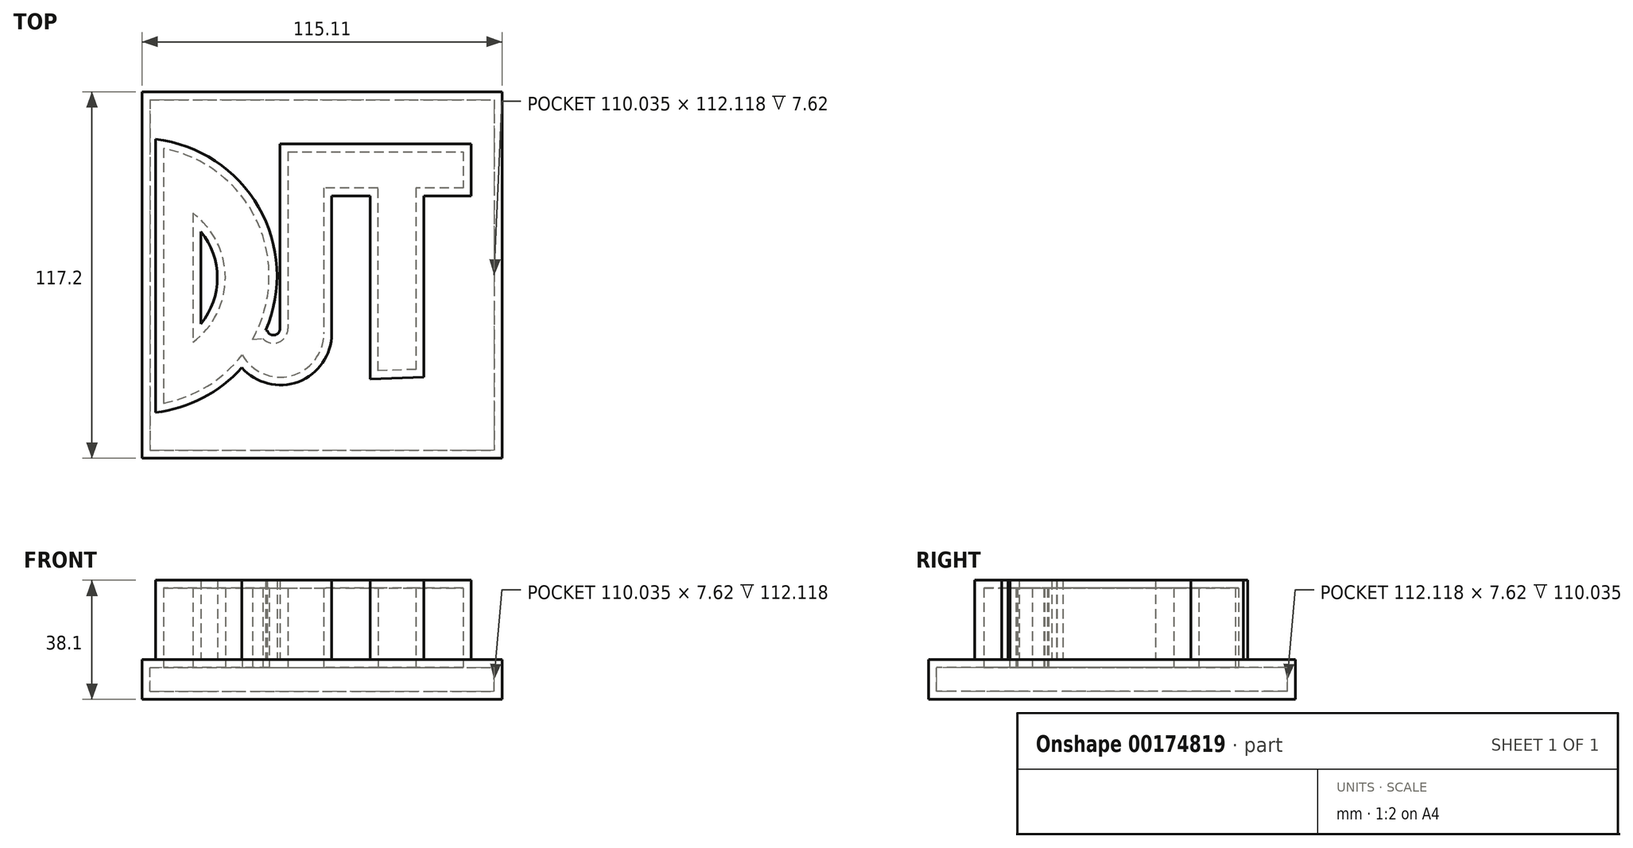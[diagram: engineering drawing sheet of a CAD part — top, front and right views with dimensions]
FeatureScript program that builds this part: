
annotation { "Feature Type Name" : "Feature", "Feature Type Description" : "" }
export const myFeature = defineFeature(function(context is Context, id is Id, definition is map)
    precondition{}
    {
        {
            var Q0;
            Q0=qCreatedBy(makeId("Top.planeOp"),FACE);
            var sketch = newSketch(context, id + "F0", { "sketchPlane" : qUnion([Q0])});
            skLineSegment(sketch, "E0.bottom", {"start": v(-57.62, 56.06) * mm, "end": v(52.41, 56.06) * mm});
            skLineSegment(sketch, "E0.top", {"start": v(-57.62, -56.06) * mm, "end": v(52.41, -56.06) * mm});
            skLineSegment(sketch, "E0.left", {"start": v(-57.62, 56.06) * mm, "end": v(-57.62, -56.06) * mm});
            skLineSegment(sketch, "E0.right", {"start": v(52.41, 56.06) * mm, "end": v(52.41, -56.06) * mm});
            skSolve(sketch);
        }
        {
            var Q0;
            Q0=makeQuery(id+"F0.imprint","IMPRINT",FACE,{"disambiguationData":[TD([[makeQuery(id+"F0.imprint","IMPRINT",EDGE,{"derivedFrom":sQuery(id+"F0.wireOp",EDGE,"E0.bottom")}),-1.0]])]});
            extrude(context, id + "F1", {"entities" : qUnion([Q0]), "oppositeDirection" : true, "depth" : 7.62 * mm});
        }
        {
            var Q0;
            Q0=qCreatedBy(makeId("Top.planeOp"),FACE);
            var sketch = newSketch(context, id + "F2", { "sketchPlane" : qUnion([Q0])});
            skLineSegment(sketch, "E1", {"start": v(-53.28, 40.44) * mm, "end": v(-53.28, -40.96) * mm});
            skArc(sketch, "E2", {"start": v(-53.28, -40.96) * mm, "mid": v(-19.55, -0.26) * mm, "end": v(-53.28, 40.44) * mm});
            skLineSegment(sketch, "E3", {"start": v(-43.91, 19.79) * mm, "end": v(-43.91, -21.52) * mm});
            skArc(sketch, "E4", {"start": v(-43.91, -21.52) * mm, "mid": v(-33.53, -0.87) * mm, "end": v(-43.91, 19.79) * mm});
            skSolve(sketch);
        }
        {
            var Q0;
            Q0=makeQuery(id+"F2.imprint","IMPRINT",FACE,{"disambiguationData":[TD([[makeQuery(id+"F2.imprint","IMPRINT",EDGE,{"derivedFrom":sQuery(id+"F2.wireOp",EDGE,"E1")}),1.0]])]});
            extrude(context, id + "F3", {"entities" : qUnion([Q0]), "operationType" : NewBodyOperationType.ADD, "depth" : 25.4 * mm});
        }
        {
            var Q0;
            Q0=qCreatedBy(makeId("Top.planeOp"),FACE);
            var sketch = newSketch(context, id + "F4", { "sketchPlane" : qUnion([Q0])});
            skLineSegment(sketch, "E5", {"start": v(-13.54, 39.4) * mm, "end": v(42.52, 39.4) * mm});
            skLineSegment(sketch, "E6", {"start": v(42.52, 39.4) * mm, "end": v(42.52, 27.77) * mm});
            skLineSegment(sketch, "E7", {"start": v(42.52, 27.77) * mm, "end": v(-2.08, 27.77) * mm});
            skLineSegment(sketch, "E8", {"start": v(-2.08, 27.77) * mm, "end": v(-2.08, -18.74) * mm});
            skLineSegment(sketch, "E9", {"start": v(-13.54, 39.4) * mm, "end": v(-13.54, -17.18) * mm});
            skLineSegment(sketch, "E10", {"start": v(15.27, -30.6) * mm, "end": v(15.27, 27.77) * mm});
            skLineSegment(sketch, "E11", {"start": v(27.42, 27.77) * mm, "end": v(27.42, -30.17) * mm});
            skLineSegment(sketch, "E12", {"start": v(27.42, -30.17) * mm, "end": v(15.27, -30.6) * mm});
            skArc(sketch, "E13", {"start": v(-29.68, -21) * mm, "mid": v(-14.84, -32.59) * mm, "end": v(-2.08, -18.74) * mm});
            skArc(sketch, "E14", {"start": v(-21.52, -20.3) * mm, "mid": v(-16.46, -21.47) * mm, "end": v(-13.54, -17.18) * mm});
            skLineSegment(sketch, "E15", {"start": v(-29.68, -21) * mm, "end": v(-21.52, -20.3) * mm});
            skSolve(sketch);
        }
        {
            var Q0;
            Q0=makeQuery(id+"F4.imprint","IMPRINT",FACE,{"disambiguationData":[TD([[makeQuery(id+"F4.imprint","IMPRINT",EDGE,{"derivedFrom":sQuery(id+"F4.wireOp",EDGE,"E5")}),-1.0]])]});
            var Q1;
            {var subQ0=sQuery(id+"F4.wireOp",EDGE,"E10");Q1=makeQuery(id+"F4.imprint","IMPRINT",FACE,{"disambiguationData":[TD([[makeQuery(id+"F4.imprint","IMPRINT",EDGE,{"derivedFrom":subQ0}),-1.0]])]});}
            extrude(context, id + "F5", {"entities" : qUnion([Q0, Q1]), "operationType" : NewBodyOperationType.ADD, "depth" : 25.4 * mm});
        }
        {
            var Q0;
            Q0=makeQuery(id+"F5.boolean.opBoolean","MERGE",FACE,{"derivedFrom":[makeQuery(id+"F3.opExtrude","CAP_FACE",FACE,{"disambiguationData":[OSD([sQuery(id+"F2.wireOp",EDGE,"E1"),sQuery(id+"F2.wireOp",EDGE,"E2"),sQuery(id+"F2.wireOp",EDGE,"E3"),sQuery(id+"F2.wireOp",EDGE,"E4")])],"isStart":false}),makeQuery(id+"F5.opExtrude","CAP_FACE",FACE,{"disambiguationData":[OSD([sQuery(id+"F4.wireOp",EDGE,"E5"),sQuery(id+"F4.wireOp",EDGE,"E6"),sQuery(id+"F4.wireOp",EDGE,"E7"),sQuery(id+"F4.wireOp",EDGE,"E8"),sQuery(id+"F4.wireOp",EDGE,"E9"),sQuery(id+"F4.wireOp",EDGE,"E10"),sQuery(id+"F4.wireOp",EDGE,"E11"),sQuery(id+"F4.wireOp",EDGE,"E12"),sQuery(id+"F4.wireOp",EDGE,"E13"),sQuery(id+"F4.wireOp",EDGE,"E14"),sQuery(id+"F4.wireOp",EDGE,"E15")])],"isStart":false})]});
            var Q1;
            Q1=makeQuery(id+"F1.opExtrude","SWEPT_BODY",BODY,{"disambiguationData":[OSD([sQuery(id+"F0.wireOp",EDGE,"E0.bottom"),sQuery(id+"F0.wireOp",EDGE,"E0.top"),sQuery(id+"F0.wireOp",EDGE,"E0.left"),sQuery(id+"F0.wireOp",EDGE,"E0.right")])]});
            shell(context, id + "F6", {"isHollow" : true, "entities" : qUnion([Q0]), "parts" : qUnion([Q1]), "thickness" : 2.54 * mm, "oppositeDirection" : true});
        }
    });
